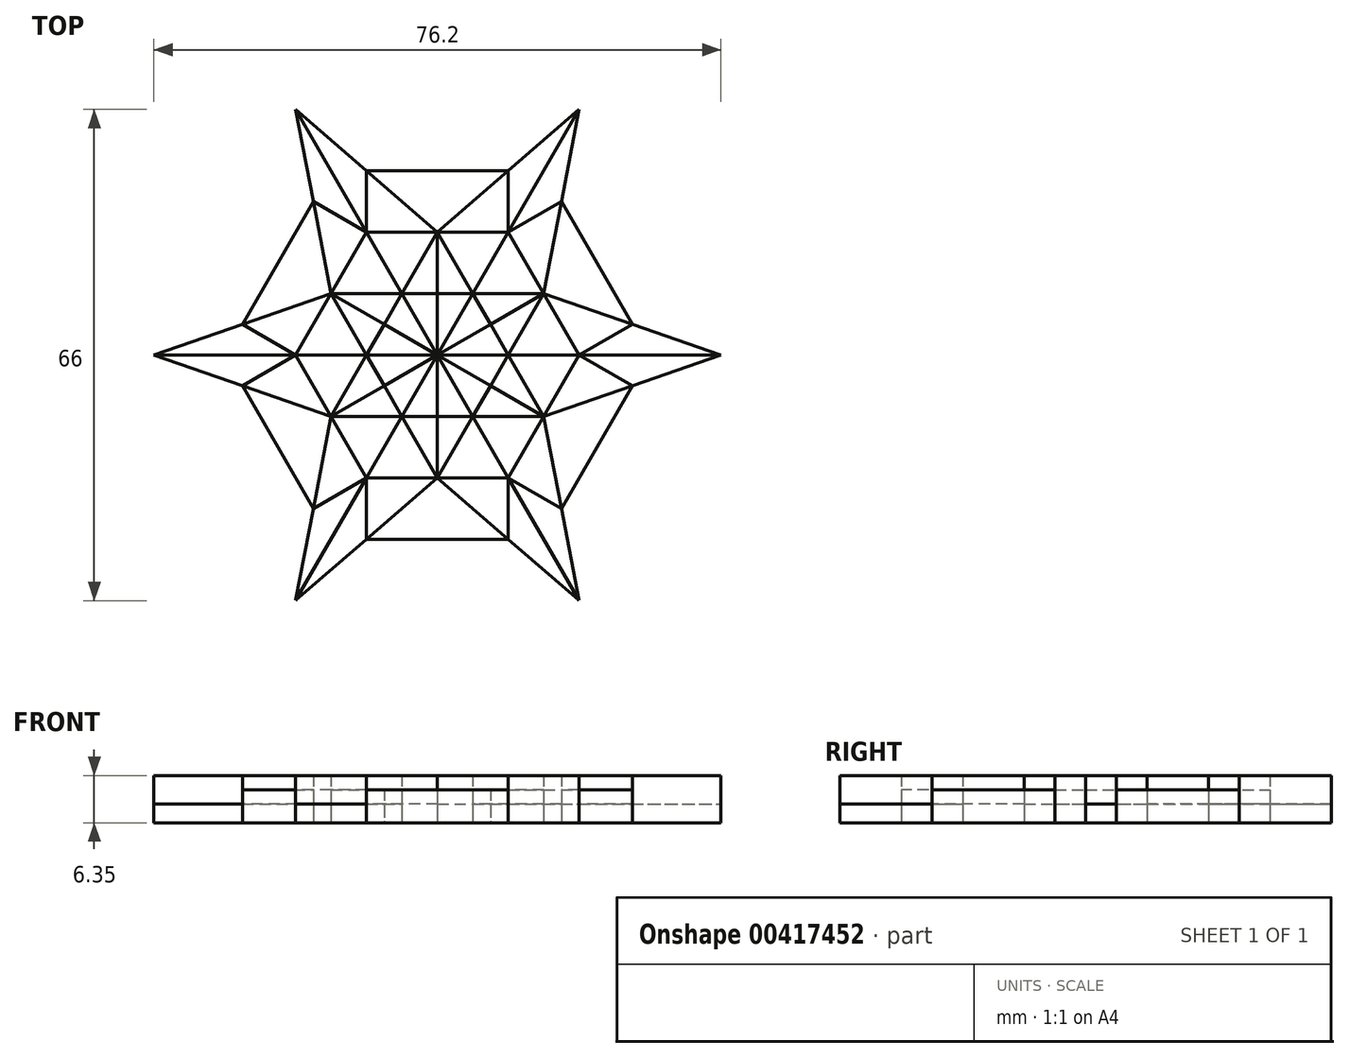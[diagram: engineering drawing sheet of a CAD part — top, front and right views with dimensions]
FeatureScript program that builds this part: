
annotation { "Feature Type Name" : "Feature", "Feature Type Description" : "" }
export const myFeature = defineFeature(function(context is Context, id is Id, definition is map)
    precondition{}
    {
        {
            var Q0;
            Q0=qCreatedBy(makeId("Top.planeOp"),FACE);
            var sketch = newSketch(context, id + "F0", { "sketchPlane" : qUnion([Q0])});
            skLineSegment(sketch, "E0.bottom", {"start": v(38.1, 50.8) * mm, "end": v(-38.1, 50.8) * mm});
            skLineSegment(sketch, "E0.top", {"start": v(38.1, -50.8) * mm, "end": v(-38.1, -50.8) * mm});
            skLineSegment(sketch, "E0.left", {"start": v(38.1, 50.8) * mm, "end": v(38.1, -50.8) * mm});
            skLineSegment(sketch, "E0.right", {"start": v(-38.1, 50.8) * mm, "end": v(-38.1, -50.8) * mm});
            skPoint(sketch, "E0.middle", {"position": v(0, 0) * mm});
            skLineSegment(sketch, "E1", {"start": v(0, 50.8) * mm, "end": v(0, -50.8) * mm});
            skLineSegment(sketch, "E2", {"start": v(-38.1, 0) * mm, "end": v(38.1, 0) * mm});
            skLineSegment(sketch, "E3.bottom", {"start": v(-38.1, 38.1) * mm, "end": v(38.1, 38.1) * mm});
            skLineSegment(sketch, "E3.top", {"start": v(-38.1, -38.1) * mm, "end": v(38.1, -38.1) * mm});
            skLineSegment(sketch, "E3.left", {"start": v(-38.1, 38.1) * mm, "end": v(-38.1, -38.1) * mm});
            skLineSegment(sketch, "E3.right", {"start": v(38.1, 38.1) * mm, "end": v(38.1, -38.1) * mm});
            skCircle(sketch, "E4", {"center": v(0, 0) * mm, "radius": 38.1 * mm});
            skLineSegment(sketch, "E5", {"start": v(-19.05, -33) * mm, "end": v(0, 0) * mm});
            skLineSegment(sketch, "E6", {"start": v(0, 0) * mm, "end": v(19.05, 33) * mm});
            skLineSegment(sketch, "E7", {"start": v(0, 0) * mm, "end": v(19.05, -33) * mm});
            skLineSegment(sketch, "E8", {"start": v(0, 0) * mm, "end": v(-19.05, 33) * mm});
            skLineSegment(sketch, "E9", {"start": v(-9.53, 16.5) * mm, "end": v(9.53, 16.5) * mm});
            skLineSegment(sketch, "E10", {"start": v(9.53, 16.5) * mm, "end": v(19.05, 0) * mm});
            skLineSegment(sketch, "E11", {"start": v(19.05, 0) * mm, "end": v(9.53, -16.5) * mm});
            skLineSegment(sketch, "E12", {"start": v(9.53, -16.5) * mm, "end": v(-9.52, -16.5) * mm});
            skLineSegment(sketch, "E13", {"start": v(-9.52, -16.5) * mm, "end": v(-19.05, 0) * mm});
            skLineSegment(sketch, "E14", {"start": v(-19.05, 0) * mm, "end": v(-9.53, 16.5) * mm});
            skLineSegment(sketch, "E15", {"start": v(-14.29, -8.25) * mm, "end": v(-19.05, -33) * mm});
            skLineSegment(sketch, "E16", {"start": v(-19.05, -33) * mm, "end": v(0, -16.5) * mm});
            skLineSegment(sketch, "E17", {"start": v(0, -16.5) * mm, "end": v(19.05, -33) * mm});
            skLineSegment(sketch, "E18", {"start": v(14.29, -8.25) * mm, "end": v(38.1, 0) * mm});
            skLineSegment(sketch, "E19", {"start": v(14.29, 8.25) * mm, "end": v(19.05, 33) * mm});
            skLineSegment(sketch, "E20", {"start": v(14.29, 8.25) * mm, "end": v(38.1, 0) * mm});
            skLineSegment(sketch, "E21", {"start": v(14.29, -8.25) * mm, "end": v(19.05, -33) * mm});
            skLineSegment(sketch, "E22", {"start": v(0, 16.5) * mm, "end": v(19.05, 33) * mm});
            skLineSegment(sketch, "E23", {"start": v(0, 16.5) * mm, "end": v(-19.05, 33) * mm});
            skLineSegment(sketch, "E24", {"start": v(-19.05, 33) * mm, "end": v(-14.29, 8.25) * mm});
            skLineSegment(sketch, "E25", {"start": v(-14.29, 8.25) * mm, "end": v(-38.1, 0) * mm});
            skLineSegment(sketch, "E26", {"start": v(-14.29, -8.25) * mm, "end": v(-38.1, 0) * mm});
            skLineSegment(sketch, "E27", {"start": v(-9.52, -24.75) * mm, "end": v(9.53, -24.75) * mm});
            skLineSegment(sketch, "E28", {"start": v(9.53, -24.75) * mm, "end": v(9.53, -16.5) * mm});
            skLineSegment(sketch, "E29", {"start": v(16.67, -20.62) * mm, "end": v(9.53, -16.5) * mm});
            skLineSegment(sketch, "E30", {"start": v(26.2, -4.12) * mm, "end": v(16.67, -20.62) * mm});
            skLineSegment(sketch, "E31", {"start": v(26.2, -4.12) * mm, "end": v(19.05, 0) * mm});
            skLineSegment(sketch, "E32", {"start": v(26.2, 4.12) * mm, "end": v(19.05, 0) * mm});
            skLineSegment(sketch, "E33", {"start": v(16.67, 20.62) * mm, "end": v(9.53, 16.5) * mm});
            skLineSegment(sketch, "E34", {"start": v(9.53, 24.75) * mm, "end": v(9.53, 16.5) * mm});
            skLineSegment(sketch, "E35", {"start": v(-9.53, 24.75) * mm, "end": v(-9.53, 16.5) * mm});
            skLineSegment(sketch, "E36", {"start": v(-16.67, 20.62) * mm, "end": v(-9.53, 16.5) * mm});
            skLineSegment(sketch, "E37", {"start": v(-26.2, 4.12) * mm, "end": v(-19.05, 0) * mm});
            skLineSegment(sketch, "E38", {"start": v(-26.2, -4.12) * mm, "end": v(-19.05, 0) * mm});
            skLineSegment(sketch, "E39", {"start": v(-9.52, -24.75) * mm, "end": v(-9.52, -16.5) * mm});
            skLineSegment(sketch, "E40", {"start": v(-16.67, -20.62) * mm, "end": v(-9.52, -16.5) * mm});
            skLineSegment(sketch, "E41", {"start": v(-16.67, -20.62) * mm, "end": v(-26.2, -4.12) * mm});
            skLineSegment(sketch, "E42", {"start": v(-26.2, 4.12) * mm, "end": v(-16.67, 20.62) * mm});
            skLineSegment(sketch, "E43", {"start": v(-9.53, 24.75) * mm, "end": v(9.53, 24.75) * mm});
            skLineSegment(sketch, "E44", {"start": v(16.67, 20.62) * mm, "end": v(26.2, 4.12) * mm});
            skLineSegment(sketch, "E45", {"start": v(-14.29, -8.25) * mm, "end": v(14.29, 8.25) * mm});
            skLineSegment(sketch, "E46", {"start": v(14.29, -8.25) * mm, "end": v(-14.29, 8.25) * mm});
            skLineSegment(sketch, "E47", {"start": v(0, -16.5) * mm, "end": v(14.29, 8.25) * mm});
            skLineSegment(sketch, "E48", {"start": v(14.29, 8.25) * mm, "end": v(-14.29, 8.25) * mm});
            skLineSegment(sketch, "E49", {"start": v(14.29, -8.25) * mm, "end": v(0, 16.5) * mm});
            skLineSegment(sketch, "E50", {"start": v(-14.29, -8.25) * mm, "end": v(14.29, -8.25) * mm});
            skLineSegment(sketch, "E51", {"start": v(0, -16.5) * mm, "end": v(-14.29, 8.25) * mm});
            skLineSegment(sketch, "E52", {"start": v(0, 16.5) * mm, "end": v(-14.29, -8.25) * mm});
            skSolve(sketch);
        }
        {
            var Q0;
            {var subQ3=sQuery(id+"F0.wireOp",EDGE,"E37");Q0=makeQuery(id+"F0.imprint","IMPRINT",FACE,{"disambiguationData":[TD([[makeQuery(id+"F0.imprint","IMPRINT",EDGE,{"derivedFrom":subQ3}),-1.0]])]});}
            var Q1;
            {var subQ3=sQuery(id+"F0.wireOp",EDGE,"E31");Q1=makeQuery(id+"F0.imprint","IMPRINT",FACE,{"disambiguationData":[TD([[makeQuery(id+"F0.imprint","IMPRINT",EDGE,{"derivedFrom":subQ3}),-1.0]])]});}
            var Q2;
            {var subQ3=sQuery(id+"F0.wireOp",EDGE,"E33");Q2=makeQuery(id+"F0.imprint","IMPRINT",FACE,{"disambiguationData":[TD([[makeQuery(id+"F0.imprint","IMPRINT",EDGE,{"derivedFrom":subQ3}),-1.0]])]});}
            var Q3;
            {var subQ3=sQuery(id+"F0.wireOp",EDGE,"E35");Q3=makeQuery(id+"F0.imprint","IMPRINT",FACE,{"disambiguationData":[TD([[makeQuery(id+"F0.imprint","IMPRINT",EDGE,{"derivedFrom":subQ3}),-1.0]])]});}
            var Q4;
            {var subQ3=sQuery(id+"F0.wireOp",EDGE,"E28");Q4=makeQuery(id+"F0.imprint","IMPRINT",FACE,{"disambiguationData":[TD([[makeQuery(id+"F0.imprint","IMPRINT",EDGE,{"derivedFrom":subQ3}),-1.0]])]});}
            var Q5;
            {var subQ3=sQuery(id+"F0.wireOp",EDGE,"E40");Q5=makeQuery(id+"F0.imprint","IMPRINT",FACE,{"disambiguationData":[TD([[makeQuery(id+"F0.imprint","IMPRINT",EDGE,{"derivedFrom":subQ3}),-1.0]])]});}
            var Q6;
            {var subQ0=sQuery(id+"F0.wireOp",EDGE,"E38");Q6=makeQuery(id+"F0.imprint","IMPRINT",FACE,{"disambiguationData":[TD([[makeQuery(id+"F0.imprint","IMPRINT",EDGE,{"derivedFrom":subQ0}),-1.0]])]});}
            var Q7;
            {var subQ0=sQuery(id+"F0.wireOp",EDGE,"E36");Q7=makeQuery(id+"F0.imprint","IMPRINT",FACE,{"disambiguationData":[TD([[makeQuery(id+"F0.imprint","IMPRINT",EDGE,{"derivedFrom":subQ0}),-1.0]])]});}
            var Q8;
            {var subQ0=sQuery(id+"F0.wireOp",EDGE,"E34");Q8=makeQuery(id+"F0.imprint","IMPRINT",FACE,{"disambiguationData":[TD([[makeQuery(id+"F0.imprint","IMPRINT",EDGE,{"derivedFrom":subQ0}),-1.0]])]});}
            var Q9;
            {var subQ0=sQuery(id+"F0.wireOp",EDGE,"E32");Q9=makeQuery(id+"F0.imprint","IMPRINT",FACE,{"disambiguationData":[TD([[makeQuery(id+"F0.imprint","IMPRINT",EDGE,{"derivedFrom":subQ0}),-1.0]])]});}
            var Q10;
            {var subQ0=sQuery(id+"F0.wireOp",EDGE,"E29");Q10=makeQuery(id+"F0.imprint","IMPRINT",FACE,{"disambiguationData":[TD([[makeQuery(id+"F0.imprint","IMPRINT",EDGE,{"derivedFrom":subQ0}),-1.0]])]});}
            var Q11;
            {var subQ0=sQuery(id+"F0.wireOp",EDGE,"E39");Q11=makeQuery(id+"F0.imprint","IMPRINT",FACE,{"disambiguationData":[TD([[makeQuery(id+"F0.imprint","IMPRINT",EDGE,{"derivedFrom":subQ0}),-1.0]])]});}
            var Q12;
            {var subQ1=sQuery(id+"F0.wireOp",EDGE,"E5");var subQ3=sQuery(id+"F0.wireOp",EDGE,"E50");var subQ4=makeQuery(id+"F0.imprint","INTERSECT",VERTEX,{"derivedFrom":[subQ1,subQ3]});Q12=makeQuery(id+"F0.imprint","IMPRINT",FACE,{"disambiguationData":[TD([[makeQuery(id+"F0.imprint","IMPRINT",EDGE,{"disambiguationData":[TD([[subQ4,1.0]])],"derivedFrom":subQ1}),1.0]])]});}
            var Q13;
            {var subQ0=sQuery(id+"F0.wireOp",EDGE,"PVZI9asG-C5Xr-yCqe-cN5U-pWch6IMBKt0i");var subQ1=sQuery(id+"F0.wireOp",EDGE,"E46");var subQ2=makeQuery(id+"F0.imprint","INTERSECT",VERTEX,{"derivedFrom":[subQ1,subQ0]});Q13=makeQuery(id+"F0.imprint","IMPRINT",FACE,{"disambiguationData":[TD([[makeQuery(id+"F0.imprint","IMPRINT",EDGE,{"disambiguationData":[TD([[subQ2,-1.0]])],"derivedFrom":subQ0}),-1.0]])]});}
            var Q14;
            {var subQ1=sQuery(id+"F0.wireOp",EDGE,"E6");var subQ3=sQuery(id+"F0.wireOp",EDGE,"E48");var subQ4=makeQuery(id+"F0.imprint","INTERSECT",VERTEX,{"derivedFrom":[subQ1,subQ3,sQuery(id+"F0.wireOp",EDGE,"E49")]});Q14=makeQuery(id+"F0.imprint","IMPRINT",FACE,{"disambiguationData":[TD([[makeQuery(id+"F0.imprint","IMPRINT",EDGE,{"disambiguationData":[TD([[subQ4,-1.0]])],"derivedFrom":subQ1}),-1.0]])]});}
            var Q15;
            {var subQ1=sQuery(id+"F0.wireOp",EDGE,"E2");var subQ3=sQuery(id+"F0.wireOp",EDGE,"E49");var subQ4=makeQuery(id+"F0.imprint","INTERSECT",VERTEX,{"derivedFrom":[subQ1,sQuery(id+"F0.wireOp",EDGE,"E47"),subQ3]});Q15=makeQuery(id+"F0.imprint","IMPRINT",FACE,{"disambiguationData":[TD([[makeQuery(id+"F0.imprint","IMPRINT",EDGE,{"disambiguationData":[TD([[subQ4,-1.0]])],"derivedFrom":subQ1}),-1.0]])]});}
            var Q16;
            {var subQ1=sQuery(id+"F0.wireOp",EDGE,"E7");var subQ3=sQuery(id+"F0.wireOp",EDGE,"E47");var subQ4=makeQuery(id+"F0.imprint","INTERSECT",VERTEX,{"derivedFrom":[subQ1,subQ3,sQuery(id+"F0.wireOp",EDGE,"E50")]});Q16=makeQuery(id+"F0.imprint","IMPRINT",FACE,{"disambiguationData":[TD([[makeQuery(id+"F0.imprint","IMPRINT",EDGE,{"disambiguationData":[TD([[subQ4,-1.0]])],"derivedFrom":subQ1}),-1.0]])]});}
            var Q17;
            {var subQ1=sQuery(id+"F0.wireOp",EDGE,"E8");var subQ3=sQuery(id+"F0.wireOp",EDGE,"E52");var subQ4=makeQuery(id+"F0.imprint","INTERSECT",VERTEX,{"derivedFrom":[subQ1,sQuery(id+"F0.wireOp",EDGE,"E48"),subQ3]});Q17=makeQuery(id+"F0.imprint","IMPRINT",FACE,{"disambiguationData":[TD([[makeQuery(id+"F0.imprint","IMPRINT",EDGE,{"disambiguationData":[TD([[subQ4,-1.0]])],"derivedFrom":subQ1}),-1.0]])]});}
            var Q18;
            {var subQ1=sQuery(id+"F0.wireOp",EDGE,"E2");var subQ3=sQuery(id+"F0.wireOp",EDGE,"E51");var subQ4=makeQuery(id+"F0.imprint","INTERSECT",VERTEX,{"derivedFrom":[subQ1,subQ3,sQuery(id+"F0.wireOp",EDGE,"E52")]});Q18=makeQuery(id+"F0.imprint","IMPRINT",FACE,{"disambiguationData":[TD([[makeQuery(id+"F0.imprint","IMPRINT",EDGE,{"disambiguationData":[TD([[subQ4,1.0]])],"derivedFrom":subQ1}),1.0]])]});}
            extrude(context, id + "F1", {"entities" : qUnion([Q0, Q1, Q2, Q3, Q4, Q5, Q6, Q7, Q8, Q9, Q10, Q11, Q12, Q13, Q14, Q15, Q16, Q17, Q18]), "depth" : 6.35 * mm});
        }
        {
            var Q0;
            {var subQ3=sQuery(id+"F0.wireOp",EDGE,"E42");Q0=makeQuery(id+"F0.imprint","IMPRINT",FACE,{"disambiguationData":[TD([[makeQuery(id+"F0.imprint","IMPRINT",EDGE,{"derivedFrom":subQ3}),-1.0]])]});}
            var Q1;
            {var subQ1=sQuery(id+"F0.wireOp",EDGE,"E1");var subQ3=sQuery(id+"F0.wireOp",EDGE,"E43");var subQ4=makeQuery(id+"F0.imprint","INTERSECT",VERTEX,{"derivedFrom":[subQ1,subQ3]});Q1=makeQuery(id+"F0.imprint","IMPRINT",FACE,{"disambiguationData":[TD([[makeQuery(id+"F0.imprint","IMPRINT",EDGE,{"disambiguationData":[TD([[subQ4,1.0]])],"derivedFrom":subQ3}),-1.0]])]});}
            var Q2;
            {var subQ1=sQuery(id+"F0.wireOp",EDGE,"E1");var subQ3=sQuery(id+"F0.wireOp",EDGE,"E43");var subQ4=makeQuery(id+"F0.imprint","INTERSECT",VERTEX,{"derivedFrom":[subQ1,subQ3]});Q2=makeQuery(id+"F0.imprint","IMPRINT",FACE,{"disambiguationData":[TD([[makeQuery(id+"F0.imprint","IMPRINT",EDGE,{"disambiguationData":[TD([[subQ4,-1.0]])],"derivedFrom":subQ3}),-1.0]])]});}
            var Q3;
            {var subQ3=sQuery(id+"F0.wireOp",EDGE,"E44");Q3=makeQuery(id+"F0.imprint","IMPRINT",FACE,{"disambiguationData":[TD([[makeQuery(id+"F0.imprint","IMPRINT",EDGE,{"derivedFrom":subQ3}),-1.0]])]});}
            var Q4;
            {var subQ1=sQuery(id+"F0.wireOp",EDGE,"E1");var subQ3=sQuery(id+"F0.wireOp",EDGE,"E27");var subQ4=makeQuery(id+"F0.imprint","INTERSECT",VERTEX,{"derivedFrom":[subQ1,subQ3]});Q4=makeQuery(id+"F0.imprint","IMPRINT",FACE,{"disambiguationData":[TD([[makeQuery(id+"F0.imprint","IMPRINT",EDGE,{"disambiguationData":[TD([[subQ4,-1.0]])],"derivedFrom":subQ3}),1.0]])]});}
            var Q5;
            {var subQ1=sQuery(id+"F0.wireOp",EDGE,"E1");var subQ3=sQuery(id+"F0.wireOp",EDGE,"E27");var subQ4=makeQuery(id+"F0.imprint","INTERSECT",VERTEX,{"derivedFrom":[subQ1,subQ3]});Q5=makeQuery(id+"F0.imprint","IMPRINT",FACE,{"disambiguationData":[TD([[makeQuery(id+"F0.imprint","IMPRINT",EDGE,{"disambiguationData":[TD([[subQ4,1.0]])],"derivedFrom":subQ3}),1.0]])]});}
            var Q6;
            {var subQ3=sQuery(id+"F0.wireOp",EDGE,"E41");Q6=makeQuery(id+"F0.imprint","IMPRINT",FACE,{"disambiguationData":[TD([[makeQuery(id+"F0.imprint","IMPRINT",EDGE,{"derivedFrom":subQ3}),-1.0]])]});}
            var Q7;
            {var subQ3=sQuery(id+"F0.wireOp",EDGE,"E30");Q7=makeQuery(id+"F0.imprint","IMPRINT",FACE,{"disambiguationData":[TD([[makeQuery(id+"F0.imprint","IMPRINT",EDGE,{"derivedFrom":subQ3}),-1.0]])]});}
            var Q8;
            {var subQ0=sQuery(id+"F0.wireOp",EDGE,"E46");var subQ3=sQuery(id+"F0.wireOp",EDGE,"E47");var subQ5=makeQuery(id+"F0.imprint","INTERSECT",VERTEX,{"derivedFrom":[subQ0,subQ3]});Q8=makeQuery(id+"F0.imprint","IMPRINT",FACE,{"disambiguationData":[TD([[makeQuery(id+"F0.imprint","IMPRINT",EDGE,{"disambiguationData":[TD([[subQ5,-1.0]])],"derivedFrom":subQ3}),1.0]])]});}
            var Q9;
            {var subQ1=sQuery(id+"F0.wireOp",EDGE,"E45");var subQ3=sQuery(id+"F0.wireOp",EDGE,"E49");var subQ4=makeQuery(id+"F0.imprint","INTERSECT",VERTEX,{"derivedFrom":[subQ1,subQ3]});Q9=makeQuery(id+"F0.imprint","IMPRINT",FACE,{"disambiguationData":[TD([[makeQuery(id+"F0.imprint","IMPRINT",EDGE,{"disambiguationData":[TD([[subQ4,1.0]])],"derivedFrom":subQ3}),-1.0]])]});}
            var Q10;
            {var subQ0=sQuery(id+"F0.wireOp",EDGE,"E45");var subQ3=sQuery(id+"F0.wireOp",EDGE,"E49");var subQ5=makeQuery(id+"F0.imprint","INTERSECT",VERTEX,{"derivedFrom":[subQ0,subQ3]});Q10=makeQuery(id+"F0.imprint","IMPRINT",FACE,{"disambiguationData":[TD([[makeQuery(id+"F0.imprint","IMPRINT",EDGE,{"disambiguationData":[TD([[subQ5,-1.0]])],"derivedFrom":subQ3}),1.0]])]});}
            var Q11;
            {var subQ1=sQuery(id+"F0.wireOp",EDGE,"E1");var subQ3=sQuery(id+"F0.wireOp",EDGE,"E48");var subQ4=makeQuery(id+"F0.imprint","INTERSECT",VERTEX,{"derivedFrom":[subQ1,subQ3]});Q11=makeQuery(id+"F0.imprint","IMPRINT",FACE,{"disambiguationData":[TD([[makeQuery(id+"F0.imprint","IMPRINT",EDGE,{"disambiguationData":[TD([[subQ4,1.0]])],"derivedFrom":subQ3}),-1.0]])]});}
            var Q12;
            {var subQ1=sQuery(id+"F0.wireOp",EDGE,"E1");var subQ3=sQuery(id+"F0.wireOp",EDGE,"E48");var subQ4=makeQuery(id+"F0.imprint","INTERSECT",VERTEX,{"derivedFrom":[subQ1,subQ3]});Q12=makeQuery(id+"F0.imprint","IMPRINT",FACE,{"disambiguationData":[TD([[makeQuery(id+"F0.imprint","IMPRINT",EDGE,{"disambiguationData":[TD([[subQ4,-1.0]])],"derivedFrom":subQ3}),1.0]])]});}
            var Q13;
            {var subQ1=sQuery(id+"F0.wireOp",EDGE,"E46");var subQ3=sQuery(id+"F0.wireOp",EDGE,"E52");var subQ4=makeQuery(id+"F0.imprint","INTERSECT",VERTEX,{"derivedFrom":[subQ1,subQ3]});Q13=makeQuery(id+"F0.imprint","IMPRINT",FACE,{"disambiguationData":[TD([[makeQuery(id+"F0.imprint","IMPRINT",EDGE,{"disambiguationData":[TD([[subQ4,1.0]])],"derivedFrom":subQ3}),-1.0]])]});}
            var Q14;
            {var subQ0=sQuery(id+"F0.wireOp",EDGE,"E46");var subQ3=sQuery(id+"F0.wireOp",EDGE,"E52");var subQ5=makeQuery(id+"F0.imprint","INTERSECT",VERTEX,{"derivedFrom":[subQ0,subQ3]});Q14=makeQuery(id+"F0.imprint","IMPRINT",FACE,{"disambiguationData":[TD([[makeQuery(id+"F0.imprint","IMPRINT",EDGE,{"disambiguationData":[TD([[subQ5,-1.0]])],"derivedFrom":subQ3}),1.0]])]});}
            var Q15;
            {var subQ1=sQuery(id+"F0.wireOp",EDGE,"E45");var subQ3=sQuery(id+"F0.wireOp",EDGE,"E51");var subQ4=makeQuery(id+"F0.imprint","INTERSECT",VERTEX,{"derivedFrom":[subQ1,subQ3]});Q15=makeQuery(id+"F0.imprint","IMPRINT",FACE,{"disambiguationData":[TD([[makeQuery(id+"F0.imprint","IMPRINT",EDGE,{"disambiguationData":[TD([[subQ4,-1.0]])],"derivedFrom":subQ3}),1.0]])]});}
            var Q16;
            {var subQ0=sQuery(id+"F0.wireOp",EDGE,"E45");var subQ3=sQuery(id+"F0.wireOp",EDGE,"E51");var subQ5=makeQuery(id+"F0.imprint","INTERSECT",VERTEX,{"derivedFrom":[subQ0,subQ3]});Q16=makeQuery(id+"F0.imprint","IMPRINT",FACE,{"disambiguationData":[TD([[makeQuery(id+"F0.imprint","IMPRINT",EDGE,{"disambiguationData":[TD([[subQ5,1.0]])],"derivedFrom":subQ3}),-1.0]])]});}
            var Q17;
            {var subQ1=sQuery(id+"F0.wireOp",EDGE,"E1");var subQ3=sQuery(id+"F0.wireOp",EDGE,"E50");var subQ4=makeQuery(id+"F0.imprint","INTERSECT",VERTEX,{"derivedFrom":[subQ1,subQ3]});Q17=makeQuery(id+"F0.imprint","IMPRINT",FACE,{"disambiguationData":[TD([[makeQuery(id+"F0.imprint","IMPRINT",EDGE,{"disambiguationData":[TD([[subQ4,1.0]])],"derivedFrom":subQ3}),-1.0]])]});}
            var Q18;
            {var subQ1=sQuery(id+"F0.wireOp",EDGE,"E1");var subQ3=sQuery(id+"F0.wireOp",EDGE,"E50");var subQ4=makeQuery(id+"F0.imprint","INTERSECT",VERTEX,{"derivedFrom":[subQ1,subQ3]});Q18=makeQuery(id+"F0.imprint","IMPRINT",FACE,{"disambiguationData":[TD([[makeQuery(id+"F0.imprint","IMPRINT",EDGE,{"disambiguationData":[TD([[subQ4,-1.0]])],"derivedFrom":subQ3}),1.0]])]});}
            var Q19;
            {var subQ1=sQuery(id+"F0.wireOp",EDGE,"E46");var subQ3=sQuery(id+"F0.wireOp",EDGE,"E47");var subQ4=makeQuery(id+"F0.imprint","INTERSECT",VERTEX,{"derivedFrom":[subQ1,subQ3]});Q19=makeQuery(id+"F0.imprint","IMPRINT",FACE,{"disambiguationData":[TD([[makeQuery(id+"F0.imprint","IMPRINT",EDGE,{"disambiguationData":[TD([[subQ4,1.0]])],"derivedFrom":subQ3}),-1.0]])]});}
            extrude(context, id + "F2", {"entities" : qUnion([Q0, Q1, Q2, Q3, Q4, Q5, Q6, Q7, Q8, Q9, Q10, Q11, Q12, Q13, Q14, Q15, Q16, Q17, Q18, Q19]), "depth" : 4.44 * mm});
        }
        {
            var Q0;
            {var subQ3=sQuery(id+"F0.wireOp",EDGE,"E38");Q0=makeQuery(id+"F0.imprint","IMPRINT",FACE,{"disambiguationData":[TD([[makeQuery(id+"F0.imprint","IMPRINT",EDGE,{"derivedFrom":subQ3}),1.0]])]});}
            var Q1;
            {var subQ3=sQuery(id+"F0.wireOp",EDGE,"E36");Q1=makeQuery(id+"F0.imprint","IMPRINT",FACE,{"disambiguationData":[TD([[makeQuery(id+"F0.imprint","IMPRINT",EDGE,{"derivedFrom":subQ3}),1.0]])]});}
            var Q2;
            {var subQ3=sQuery(id+"F0.wireOp",EDGE,"E34");Q2=makeQuery(id+"F0.imprint","IMPRINT",FACE,{"disambiguationData":[TD([[makeQuery(id+"F0.imprint","IMPRINT",EDGE,{"derivedFrom":subQ3}),1.0]])]});}
            var Q3;
            {var subQ3=sQuery(id+"F0.wireOp",EDGE,"E32");Q3=makeQuery(id+"F0.imprint","IMPRINT",FACE,{"disambiguationData":[TD([[makeQuery(id+"F0.imprint","IMPRINT",EDGE,{"derivedFrom":subQ3}),1.0]])]});}
            var Q4;
            {var subQ3=sQuery(id+"F0.wireOp",EDGE,"E29");Q4=makeQuery(id+"F0.imprint","IMPRINT",FACE,{"disambiguationData":[TD([[makeQuery(id+"F0.imprint","IMPRINT",EDGE,{"derivedFrom":subQ3}),1.0]])]});}
            var Q5;
            {var subQ3=sQuery(id+"F0.wireOp",EDGE,"E39");Q5=makeQuery(id+"F0.imprint","IMPRINT",FACE,{"disambiguationData":[TD([[makeQuery(id+"F0.imprint","IMPRINT",EDGE,{"derivedFrom":subQ3}),1.0]])]});}
            var Q6;
            {var subQ0=sQuery(id+"F0.wireOp",EDGE,"E40");Q6=makeQuery(id+"F0.imprint","IMPRINT",FACE,{"disambiguationData":[TD([[makeQuery(id+"F0.imprint","IMPRINT",EDGE,{"derivedFrom":subQ0}),1.0]])]});}
            var Q7;
            {var subQ0=sQuery(id+"F0.wireOp",EDGE,"E37");Q7=makeQuery(id+"F0.imprint","IMPRINT",FACE,{"disambiguationData":[TD([[makeQuery(id+"F0.imprint","IMPRINT",EDGE,{"derivedFrom":subQ0}),1.0]])]});}
            var Q8;
            {var subQ0=sQuery(id+"F0.wireOp",EDGE,"E35");Q8=makeQuery(id+"F0.imprint","IMPRINT",FACE,{"disambiguationData":[TD([[makeQuery(id+"F0.imprint","IMPRINT",EDGE,{"derivedFrom":subQ0}),1.0]])]});}
            var Q9;
            {var subQ0=sQuery(id+"F0.wireOp",EDGE,"E33");Q9=makeQuery(id+"F0.imprint","IMPRINT",FACE,{"disambiguationData":[TD([[makeQuery(id+"F0.imprint","IMPRINT",EDGE,{"derivedFrom":subQ0}),1.0]])]});}
            var Q10;
            {var subQ0=sQuery(id+"F0.wireOp",EDGE,"E31");Q10=makeQuery(id+"F0.imprint","IMPRINT",FACE,{"disambiguationData":[TD([[makeQuery(id+"F0.imprint","IMPRINT",EDGE,{"derivedFrom":subQ0}),1.0]])]});}
            var Q11;
            {var subQ0=sQuery(id+"F0.wireOp",EDGE,"E28");Q11=makeQuery(id+"F0.imprint","IMPRINT",FACE,{"disambiguationData":[TD([[makeQuery(id+"F0.imprint","IMPRINT",EDGE,{"derivedFrom":subQ0}),1.0]])]});}
            var Q12;
            {var subQ1=sQuery(id+"F0.wireOp",EDGE,"E5");var subQ3=sQuery(id+"F0.wireOp",EDGE,"E51");var subQ4=makeQuery(id+"F0.imprint","INTERSECT",VERTEX,{"derivedFrom":[subQ1,sQuery(id+"F0.wireOp",EDGE,"E50"),subQ3]});Q12=makeQuery(id+"F0.imprint","IMPRINT",FACE,{"disambiguationData":[TD([[makeQuery(id+"F0.imprint","IMPRINT",EDGE,{"disambiguationData":[TD([[subQ4,1.0]])],"derivedFrom":subQ1}),-1.0]])]});}
            var Q13;
            {var subQ1=sQuery(id+"F0.wireOp",EDGE,"E2");var subQ3=sQuery(id+"F0.wireOp",EDGE,"E52");var subQ4=makeQuery(id+"F0.imprint","INTERSECT",VERTEX,{"derivedFrom":[subQ1,sQuery(id+"F0.wireOp",EDGE,"E51"),subQ3]});Q13=makeQuery(id+"F0.imprint","IMPRINT",FACE,{"disambiguationData":[TD([[makeQuery(id+"F0.imprint","IMPRINT",EDGE,{"disambiguationData":[TD([[subQ4,1.0]])],"derivedFrom":subQ1}),-1.0]])]});}
            var Q14;
            {var subQ1=sQuery(id+"F0.wireOp",EDGE,"E8");var subQ3=sQuery(id+"F0.wireOp",EDGE,"E48");var subQ4=makeQuery(id+"F0.imprint","INTERSECT",VERTEX,{"derivedFrom":[subQ1,subQ3,sQuery(id+"F0.wireOp",EDGE,"E52")]});Q14=makeQuery(id+"F0.imprint","IMPRINT",FACE,{"disambiguationData":[TD([[makeQuery(id+"F0.imprint","IMPRINT",EDGE,{"disambiguationData":[TD([[subQ4,-1.0]])],"derivedFrom":subQ1}),1.0]])]});}
            var Q15;
            {var subQ1=sQuery(id+"F0.wireOp",EDGE,"E6");var subQ3=sQuery(id+"F0.wireOp",EDGE,"E49");var subQ4=makeQuery(id+"F0.imprint","INTERSECT",VERTEX,{"derivedFrom":[subQ1,sQuery(id+"F0.wireOp",EDGE,"E48"),subQ3]});Q15=makeQuery(id+"F0.imprint","IMPRINT",FACE,{"disambiguationData":[TD([[makeQuery(id+"F0.imprint","IMPRINT",EDGE,{"disambiguationData":[TD([[subQ4,-1.0]])],"derivedFrom":subQ1}),1.0]])]});}
            var Q16;
            {var subQ1=sQuery(id+"F0.wireOp",EDGE,"E2");var subQ3=sQuery(id+"F0.wireOp",EDGE,"E47");var subQ4=makeQuery(id+"F0.imprint","INTERSECT",VERTEX,{"derivedFrom":[subQ1,subQ3,sQuery(id+"F0.wireOp",EDGE,"E49")]});Q16=makeQuery(id+"F0.imprint","IMPRINT",FACE,{"disambiguationData":[TD([[makeQuery(id+"F0.imprint","IMPRINT",EDGE,{"disambiguationData":[TD([[subQ4,-1.0]])],"derivedFrom":subQ1}),1.0]])]});}
            var Q17;
            {var subQ1=sQuery(id+"F0.wireOp",EDGE,"E7");var subQ3=sQuery(id+"F0.wireOp",EDGE,"E50");var subQ4=makeQuery(id+"F0.imprint","INTERSECT",VERTEX,{"derivedFrom":[subQ1,sQuery(id+"F0.wireOp",EDGE,"E47"),subQ3]});Q17=makeQuery(id+"F0.imprint","IMPRINT",FACE,{"disambiguationData":[TD([[makeQuery(id+"F0.imprint","IMPRINT",EDGE,{"disambiguationData":[TD([[subQ4,-1.0]])],"derivedFrom":subQ1}),1.0]])]});}
            var Q18;
            {var subQ1=sQuery(id+"F0.wireOp",EDGE,"E46");var subQ3=sQuery(id+"F0.wireOp",EDGE,"E47");var subQ4=makeQuery(id+"F0.imprint","INTERSECT",VERTEX,{"derivedFrom":[subQ1,subQ3]});Q18=makeQuery(id+"F0.imprint","IMPRINT",FACE,{"disambiguationData":[TD([[makeQuery(id+"F0.imprint","IMPRINT",EDGE,{"disambiguationData":[TD([[subQ4,-1.0]])],"derivedFrom":subQ3}),-1.0]])]});}
            var Q19;
            {var subQ1=sQuery(id+"F0.wireOp",EDGE,"E45");var subQ3=sQuery(id+"F0.wireOp",EDGE,"E49");var subQ4=makeQuery(id+"F0.imprint","INTERSECT",VERTEX,{"derivedFrom":[subQ1,subQ3]});Q19=makeQuery(id+"F0.imprint","IMPRINT",FACE,{"disambiguationData":[TD([[makeQuery(id+"F0.imprint","IMPRINT",EDGE,{"disambiguationData":[TD([[subQ4,-1.0]])],"derivedFrom":subQ3}),-1.0]])]});}
            var Q20;
            {var subQ1=sQuery(id+"F0.wireOp",EDGE,"E1");var subQ3=sQuery(id+"F0.wireOp",EDGE,"E48");var subQ4=makeQuery(id+"F0.imprint","INTERSECT",VERTEX,{"derivedFrom":[subQ1,subQ3]});Q20=makeQuery(id+"F0.imprint","IMPRINT",FACE,{"disambiguationData":[TD([[makeQuery(id+"F0.imprint","IMPRINT",EDGE,{"disambiguationData":[TD([[subQ4,-1.0]])],"derivedFrom":subQ3}),-1.0]])]});}
            var Q21;
            {var subQ1=sQuery(id+"F0.wireOp",EDGE,"E46");var subQ3=sQuery(id+"F0.wireOp",EDGE,"E52");var subQ4=makeQuery(id+"F0.imprint","INTERSECT",VERTEX,{"derivedFrom":[subQ1,subQ3]});Q21=makeQuery(id+"F0.imprint","IMPRINT",FACE,{"disambiguationData":[TD([[makeQuery(id+"F0.imprint","IMPRINT",EDGE,{"disambiguationData":[TD([[subQ4,-1.0]])],"derivedFrom":subQ3}),-1.0]])]});}
            var Q22;
            {var subQ1=sQuery(id+"F0.wireOp",EDGE,"E45");var subQ3=sQuery(id+"F0.wireOp",EDGE,"E51");var subQ4=makeQuery(id+"F0.imprint","INTERSECT",VERTEX,{"derivedFrom":[subQ1,subQ3]});Q22=makeQuery(id+"F0.imprint","IMPRINT",FACE,{"disambiguationData":[TD([[makeQuery(id+"F0.imprint","IMPRINT",EDGE,{"disambiguationData":[TD([[subQ4,1.0]])],"derivedFrom":subQ3}),1.0]])]});}
            var Q23;
            {var subQ1=sQuery(id+"F0.wireOp",EDGE,"E1");var subQ3=sQuery(id+"F0.wireOp",EDGE,"E50");var subQ4=makeQuery(id+"F0.imprint","INTERSECT",VERTEX,{"derivedFrom":[subQ1,subQ3]});Q23=makeQuery(id+"F0.imprint","IMPRINT",FACE,{"disambiguationData":[TD([[makeQuery(id+"F0.imprint","IMPRINT",EDGE,{"disambiguationData":[TD([[subQ4,-1.0]])],"derivedFrom":subQ3}),-1.0]])]});}
            extrude(context, id + "F3", {"entities" : qUnion([Q0, Q1, Q2, Q3, Q4, Q5, Q6, Q7, Q8, Q9, Q10, Q11, Q12, Q13, Q14, Q15, Q16, Q17, Q18, Q19, Q20, Q21, Q22, Q23]), "depth" : 2.54 * mm});
        }
    });
